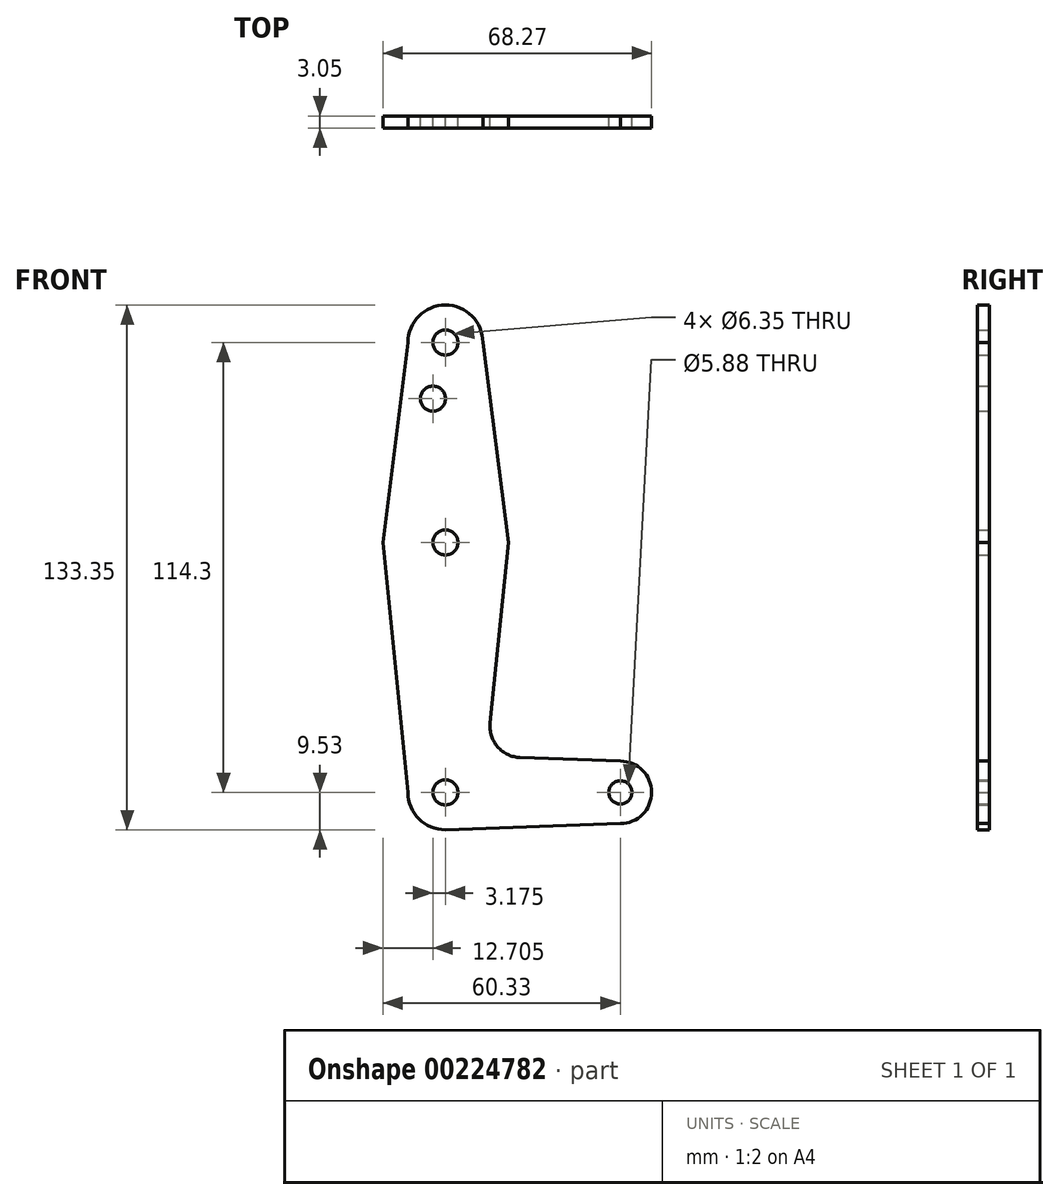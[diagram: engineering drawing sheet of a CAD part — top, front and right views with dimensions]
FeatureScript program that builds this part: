
annotation { "Feature Type Name" : "Feature", "Feature Type Description" : "" }
export const myFeature = defineFeature(function(context is Context, id is Id, definition is map)
    precondition{}
    {
        {
            var Q0;
            Q0=qCreatedBy(makeId("Front.planeOp"),FACE);
            var sketch = newSketch(context, id + "F0", { "sketchPlane" : qUnion([Q0])});
            skCircle(sketch, "E0", {"center": v(0, 0) * mm, "radius": 15.88 * mm});
            skLineSegment(sketch, "E1", {"start": v(0, 0) * mm, "end": v(0, 50.8) * mm});
            skLineSegment(sketch, "E2", {"start": v(0, 0) * mm, "end": v(0, -63.5) * mm});
            skLineSegment(sketch, "E3", {"start": v(0, -63.5) * mm, "end": v(44.45, -63.5) * mm});
            skCircle(sketch, "E4", {"center": v(0, 50.8) * mm, "radius": 9.53 * mm});
            skCircle(sketch, "E5", {"center": v(0, -63.5) * mm, "radius": 9.53 * mm});
            skCircle(sketch, "E6", {"center": v(44.45, -63.5) * mm, "radius": 7.94 * mm});
            skLineSegment(sketch, "E7", {"start": v(9.52, 50.8) * mm, "end": v(16, 0) * mm});
            skLineSegment(sketch, "E8", {"start": v(16, 0) * mm, "end": v(11.36, -45.9) * mm});
            skLineSegment(sketch, "E9", {"start": v(-15.88, 0) * mm, "end": v(-9.53, 50.8) * mm});
            skLineSegment(sketch, "E10", {"start": v(-15.88, 0) * mm, "end": v(-9.52, -63.5) * mm});
            skLineSegment(sketch, "E11", {"start": v(44.45, -55.56) * mm, "end": v(18.98, -54.65) * mm});
            skLineSegment(sketch, "E12", {"start": v(0, -73.02) * mm, "end": v(44.45, -71.44) * mm});
            skCircle(sketch, "E13", {"center": v(0, 50.8) * mm, "radius": 3.18 * mm});
            skCircle(sketch, "E14", {"center": v(0, 0) * mm, "radius": 3.18 * mm});
            skCircle(sketch, "E15", {"center": v(0, -63.5) * mm, "radius": 3.18 * mm});
            skCircle(sketch, "E16", {"center": v(44.45, -63.5) * mm, "radius": 2.94 * mm});
            skCircle(sketch, "E17", {"center": v(-3.18, 36.53) * mm, "radius": 3.18 * mm});
            skArc(sketch, "E18.filletArc", {"start": v(11.36, -45.9) * mm, "mid": v(13.27, -51.93) * mm, "end": v(18.98, -54.65) * mm});
            skSolve(sketch);
        }
        {
            var Q0;
            Q0=makeQuery(id+"F0.imprint","IMPRINT",FACE,{"disambiguationData":[TD([[makeQuery(id+"F0.imprint","IMPRINT",EDGE,{"derivedFrom":sQuery(id+"F0.wireOp",EDGE,"E13")}),-1.0]])]});
            var Q1;
            {var subQ5=sQuery(id+"F0.wireOp",EDGE,"E17");Q1=makeQuery(id+"F0.imprint","IMPRINT",FACE,{"disambiguationData":[TD([[makeQuery(id+"F0.imprint","IMPRINT",EDGE,{"derivedFrom":subQ5}),-1.0]])]});}
            var Q2;
            {var subQ0=sQuery(id+"F0.wireOp",EDGE,"E7");var subQ5=sQuery(id+"F0.wireOp",EDGE,"E0");var subQ6=makeQuery(id+"F0.imprint","INTERSECT",VERTEX,{"derivedFrom":[subQ5,subQ0]});Q2=makeQuery(id+"F0.imprint","IMPRINT",FACE,{"disambiguationData":[TD([[makeQuery(id+"F0.imprint","IMPRINT",EDGE,{"disambiguationData":[TD([[subQ6,-1.0]])],"derivedFrom":subQ5}),-1.0]])]});}
            var Q3;
            {var subQ1=sQuery(id+"F0.wireOp",EDGE,"E0");var subQ8=makeQuery(id+"F0.imprint","INTERSECT",VERTEX,{"derivedFrom":[subQ1,sQuery(id+"F0.wireOp",EDGE,"E7")]});Q3=makeQuery(id+"F0.imprint","IMPRINT",FACE,{"disambiguationData":[TD([[makeQuery(id+"F0.imprint","IMPRINT",EDGE,{"disambiguationData":[TD([[subQ8,-1.0]])],"derivedFrom":subQ1}),1.0]])]});}
            var Q4;
            {var subQ1=sQuery(id+"F0.wireOp",EDGE,"E0");var subQ6=sQuery(id+"F0.wireOp",EDGE,"E9");var subQ12=makeQuery(id+"F0.imprint","INTERSECT",VERTEX,{"derivedFrom":[subQ1,subQ6]});Q4=makeQuery(id+"F0.imprint","IMPRINT",FACE,{"disambiguationData":[TD([[makeQuery(id+"F0.imprint","IMPRINT",EDGE,{"disambiguationData":[TD([[subQ12,1.0]])],"derivedFrom":subQ1}),1.0]])]});}
            var Q5;
            {var subQ0=sQuery(id+"F0.wireOp",EDGE,"E10");var subQ1=sQuery(id+"F0.wireOp",EDGE,"E0");var subQ2=makeQuery(id+"F0.imprint","INTERSECT",VERTEX,{"derivedFrom":[subQ1,subQ0]});Q5=makeQuery(id+"F0.imprint","IMPRINT",FACE,{"disambiguationData":[TD([[makeQuery(id+"F0.imprint","IMPRINT",EDGE,{"disambiguationData":[TD([[subQ2,-1.0]])],"derivedFrom":subQ1}),-1.0]])]});}
            var Q6;
            {var subQ5=sQuery(id+"F0.wireOp",EDGE,"E8");Q6=makeQuery(id+"F0.imprint","IMPRINT",FACE,{"disambiguationData":[TD([[makeQuery(id+"F0.imprint","IMPRINT",EDGE,{"derivedFrom":subQ5}),-1.0]])]});}
            var Q7;
            {var subQ0=sQuery(id+"F0.wireOp",EDGE,"E5");var subQ1=sQuery(id+"F0.wireOp",EDGE,"E2");var subQ2=makeQuery(id+"F0.imprint","INTERSECT",VERTEX,{"derivedFrom":[subQ1,subQ0]});Q7=makeQuery(id+"F0.imprint","IMPRINT",FACE,{"disambiguationData":[TD([[makeQuery(id+"F0.imprint","IMPRINT",EDGE,{"disambiguationData":[TD([[subQ2,-1.0]])],"derivedFrom":subQ1}),1.0]])]});}
            var Q8;
            {var subQ0=sQuery(id+"F0.wireOp",EDGE,"E5");var subQ2=sQuery(id+"F0.wireOp",EDGE,"E2");var subQ3=makeQuery(id+"F0.imprint","INTERSECT",VERTEX,{"derivedFrom":[subQ2,subQ0]});Q8=makeQuery(id+"F0.imprint","IMPRINT",FACE,{"disambiguationData":[TD([[makeQuery(id+"F0.imprint","IMPRINT",EDGE,{"disambiguationData":[TD([[subQ3,-1.0]])],"derivedFrom":subQ2}),-1.0]])]});}
            var Q9;
            {var subQ0=sQuery(id+"F0.wireOp",EDGE,"E6");var subQ1=sQuery(id+"F0.wireOp",EDGE,"E3");var subQ2=makeQuery(id+"F0.imprint","INTERSECT",VERTEX,{"derivedFrom":[subQ1,subQ0]});Q9=makeQuery(id+"F0.imprint","IMPRINT",FACE,{"disambiguationData":[TD([[makeQuery(id+"F0.imprint","IMPRINT",EDGE,{"disambiguationData":[TD([[subQ2,1.0]])],"derivedFrom":subQ1}),-1.0]])]});}
            var Q10;
            Q10=makeQuery(id+"F0.imprint","IMPRINT",FACE,{"disambiguationData":[TD([[makeQuery(id+"F0.imprint","IMPRINT",EDGE,{"derivedFrom":sQuery(id+"F0.wireOp",EDGE,"E16")}),-1.0]])]});
            extrude(context, id + "F1", {"entities" : qUnion([Q0, Q1, Q2, Q3, Q4, Q5, Q6, Q7, Q8, Q9, Q10]), "depth" : 3.05 * mm});
        }
    });
